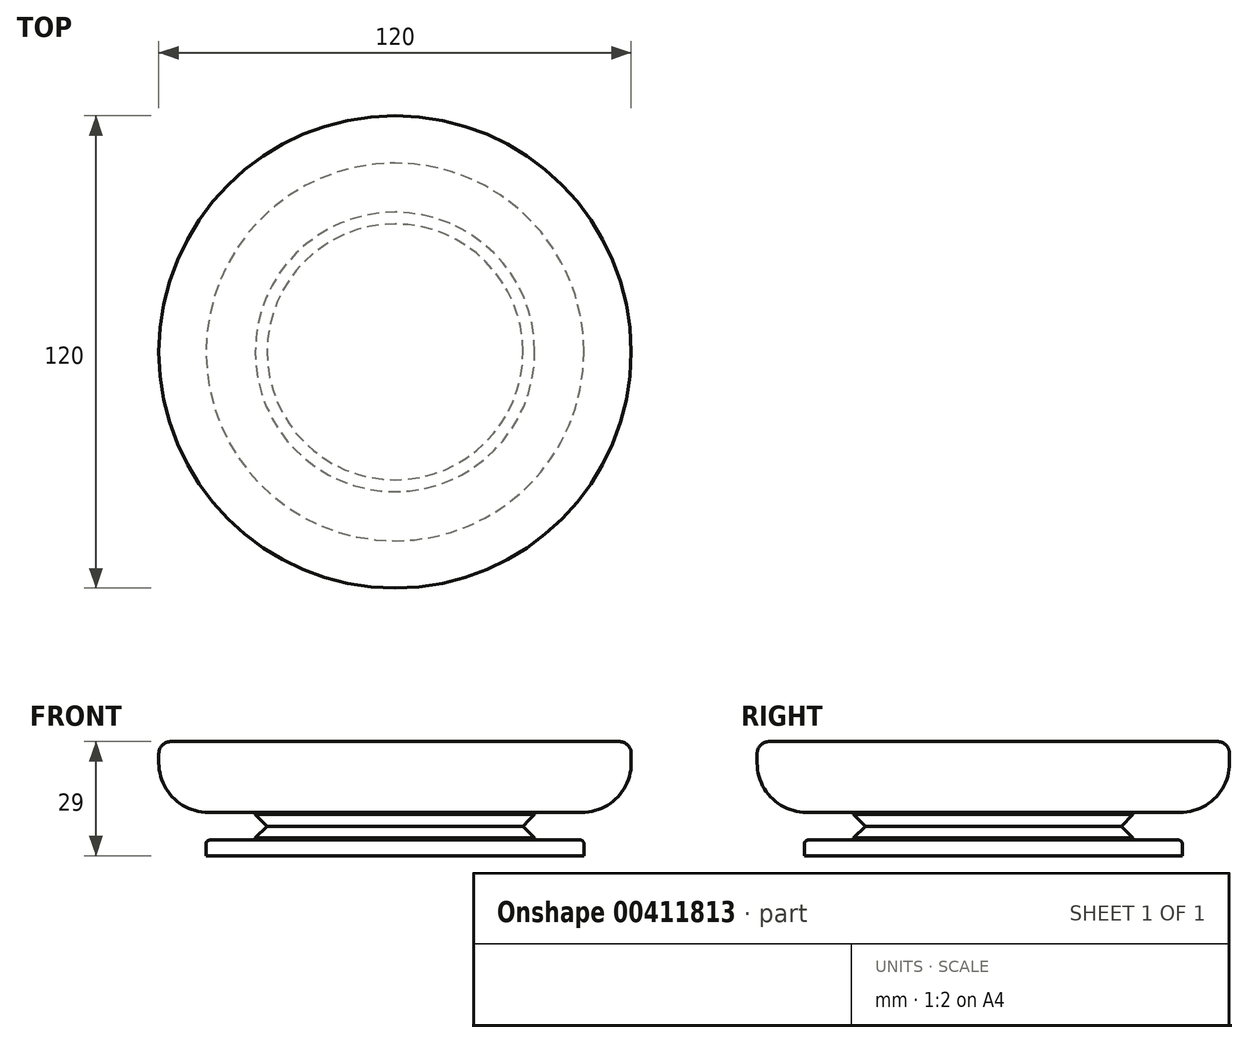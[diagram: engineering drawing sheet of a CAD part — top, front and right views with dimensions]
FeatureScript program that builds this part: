
annotation { "Feature Type Name" : "Feature", "Feature Type Description" : "" }
export const myFeature = defineFeature(function(context is Context, id is Id, definition is map)
    precondition{}
    {
        {
            var Q0;
            Q0=qCreatedBy(makeId("Top.planeOp"),FACE);
            var sketch = newSketch(context, id + "F0", { "sketchPlane" : qUnion([Q0])});
            skCircle(sketch, "E0", {"center": v(0, 0) * mm, "radius": 48 * mm});
            skSolve(sketch);
        }
        {
            var Q0;
            Q0=makeQuery(id+"F0.imprint","IMPRINT",FACE,{"disambiguationData":[TD([[makeQuery(id+"F0.imprint","IMPRINT",EDGE,{"derivedFrom":sQuery(id+"F0.wireOp",EDGE,"E0")}),1.0]])]});
            extrude(context, id + "F1", {"entities" : qUnion([Q0]), "depth" : 4 * mm, "offsetDistance" : 25 * mm});
        }
        {
            var Q0;
            Q0=makeQuery(id+"F1.opExtrude","CAP_EDGE",EDGE,{"disambiguationData":[OSD([sQuery(id+"F0.wireOp",EDGE,"E0")])],"isStart":false});
            fillet(context, id + "F2", {"entities" : qUnion([Q0]), "radius" : 1 * mm, "tangentPropagation" : true, "allowEdgeOverflow" : false});
        }
        {
            var Q0;
            Q0=makeQuery(id+"F1.opExtrude","CAP_FACE",FACE,{"disambiguationData":[OSD([sQuery(id+"F0.wireOp",EDGE,"E0")])],"isStart":false});
            var sketch = newSketch(context, id + "F3", { "sketchPlane" : qUnion([Q0])});
            skCircle(sketch, "E1", {"center": v(0, 0) * mm, "radius": 35.5 * mm});
            skSolve(sketch);
        }
        {
            var Q0;
            Q0=makeQuery(id+"F3.imprint","IMPRINT",FACE,{"disambiguationData":[TD([[makeQuery(id+"F3.imprint","IMPRINT",EDGE,{"derivedFrom":sQuery(id+"F3.wireOp",EDGE,"E1")}),1.0]])]});
            extrude(context, id + "F4", {"entities" : qUnion([Q0]), "operationType" : NewBodyOperationType.ADD, "depth" : 3.5 * mm, "offsetDistance" : 25 * mm});
        }
        {
            var Q0;
            Q0=makeQuery(id+"F4.opExtrude","CAP_EDGE",EDGE,{"disambiguationData":[OSD([sQuery(id+"F3.wireOp",EDGE,"E1")])],"isStart":false});
            chamfer(context, id + "F5", {"entities" : qUnion([Q0]), "width" : 3 * mm, "tangentPropagation" : true});
        }
        {
            var Q0;
            Q0=makeQuery(id+"F4.opExtrude","CAP_FACE",FACE,{"disambiguationData":[OSD([sQuery(id+"F3.wireOp",EDGE,"E1")])],"isStart":false});
            var sketch = newSketch(context, id + "F6", { "sketchPlane" : qUnion([Q0])});
            skCircle(sketch, "E2", {"center": v(0, 0) * mm, "radius": 35.5 * mm});
            skSolve(sketch);
        }
        {
            var Q0;
            Q0=makeQuery(id+"F6.imprint","IMPRINT",FACE,{"disambiguationData":[TD([[makeQuery(id+"F6.imprint","IMPRINT",EDGE,{"derivedFrom":sQuery(id+"F6.wireOp",EDGE,"E2")}),1.0]])]});
            var Q1;
            {var subQ0=sQuery(id+"F3.wireOp",EDGE,"E1");Q1=makeQuery(id+"F6.imprint","IMPRINT",FACE,{"disambiguationData":[TD([[makeQuery(id+"F6.imprint","IMPRINT",EDGE,{"derivedFrom":makeQuery(id+"F5.opChamfer","BLEND_EDGE",EDGE,{"blendedFrom":[makeQuery(id+"F4.opExtrude","CAP_EDGE",EDGE,{"disambiguationData":[OSD([subQ0])],"isStart":false}),makeQuery(id+"F4.opExtrude","CAP_FACE",FACE,{"disambiguationData":[OSD([subQ0])],"isStart":false})],"blendedInto":[makeQuery(id+"F4.opExtrude","CAP_FACE",FACE,{"disambiguationData":[OSD([subQ0])],"isStart":false})]})}),1.0]])]});}
            extrude(context, id + "F7", {"entities" : qUnion([Q0, Q1]), "operationType" : NewBodyOperationType.ADD, "depth" : 3.5 * mm, "offsetDistance" : 25 * mm});
        }
        {
            var Q0;
            Q0=makeQuery(id+"F7.opExtrude","CAP_EDGE",EDGE,{"disambiguationData":[OSD([sQuery(id+"F6.wireOp",EDGE,"E2")])],"isStart":true});
            chamfer(context, id + "F8", {"entities" : qUnion([Q0]), "width" : 3 * mm, "tangentPropagation" : true});
        }
        {
            var Q0;
            Q0=makeQuery(id+"F7.opExtrude","CAP_FACE",FACE,{"disambiguationData":[OSD([sQuery(id+"F6.wireOp",EDGE,"E2")])],"isStart":false});
            var sketch = newSketch(context, id + "F9", { "sketchPlane" : qUnion([Q0])});
            skCircle(sketch, "E3", {"center": v(0, 0) * mm, "radius": 60 * mm});
            skCircle(sketch, "E4", {"center": v(0, 0) * mm, "radius": 47 * mm});
            skSolve(sketch);
        }
        {
            var Q0;
            Q0=makeQuery(id+"F9.imprint","IMPRINT",FACE,{"disambiguationData":[TD([[makeQuery(id+"F9.imprint","IMPRINT",EDGE,{"derivedFrom":sQuery(id+"F9.wireOp",EDGE,"E3")}),1.0]])]});
            var Q1;
            Q1=makeQuery(id+"F9.imprint","IMPRINT",FACE,{"disambiguationData":[TD([[makeQuery(id+"F9.imprint","IMPRINT",EDGE,{"derivedFrom":makeQuery(id+"F7.opExtrude","CAP_EDGE",EDGE,{"disambiguationData":[OSD([sQuery(id+"F6.wireOp",EDGE,"E2")])],"isStart":false})}),1.0]])]});
            var Q2;
            Q2=makeQuery(id+"F9.imprint","IMPRINT",FACE,{"disambiguationData":[TD([[makeQuery(id+"F9.imprint","IMPRINT",EDGE,{"derivedFrom":sQuery(id+"F9.wireOp",EDGE,"E4")}),1.0]])]});
            extrude(context, id + "F10", {"entities" : qUnion([Q0, Q1, Q2]), "operationType" : NewBodyOperationType.ADD, "depth" : 18 * mm, "offsetDistance" : 25 * mm});
        }
        {
            var Q0;
            Q0=makeQuery(id+"F10.opExtrude","CAP_EDGE",EDGE,{"disambiguationData":[OSD([sQuery(id+"F9.wireOp",EDGE,"E3")])],"isStart":true});
            fillet(context, id + "F11", {"entities" : qUnion([Q0]), "radius" : 12.55 * mm, "tangentPropagation" : true, "allowEdgeOverflow" : false});
        }
        {
            var Q0;
            Q0=makeQuery(id+"F10.opExtrude","CAP_EDGE",EDGE,{"disambiguationData":[OSD([sQuery(id+"F9.wireOp",EDGE,"E3")])],"isStart":false});
            fillet(context, id + "F12", {"entities" : qUnion([Q0]), "radius" : 3 * mm, "tangentPropagation" : true, "allowEdgeOverflow" : false});
        }
    });
